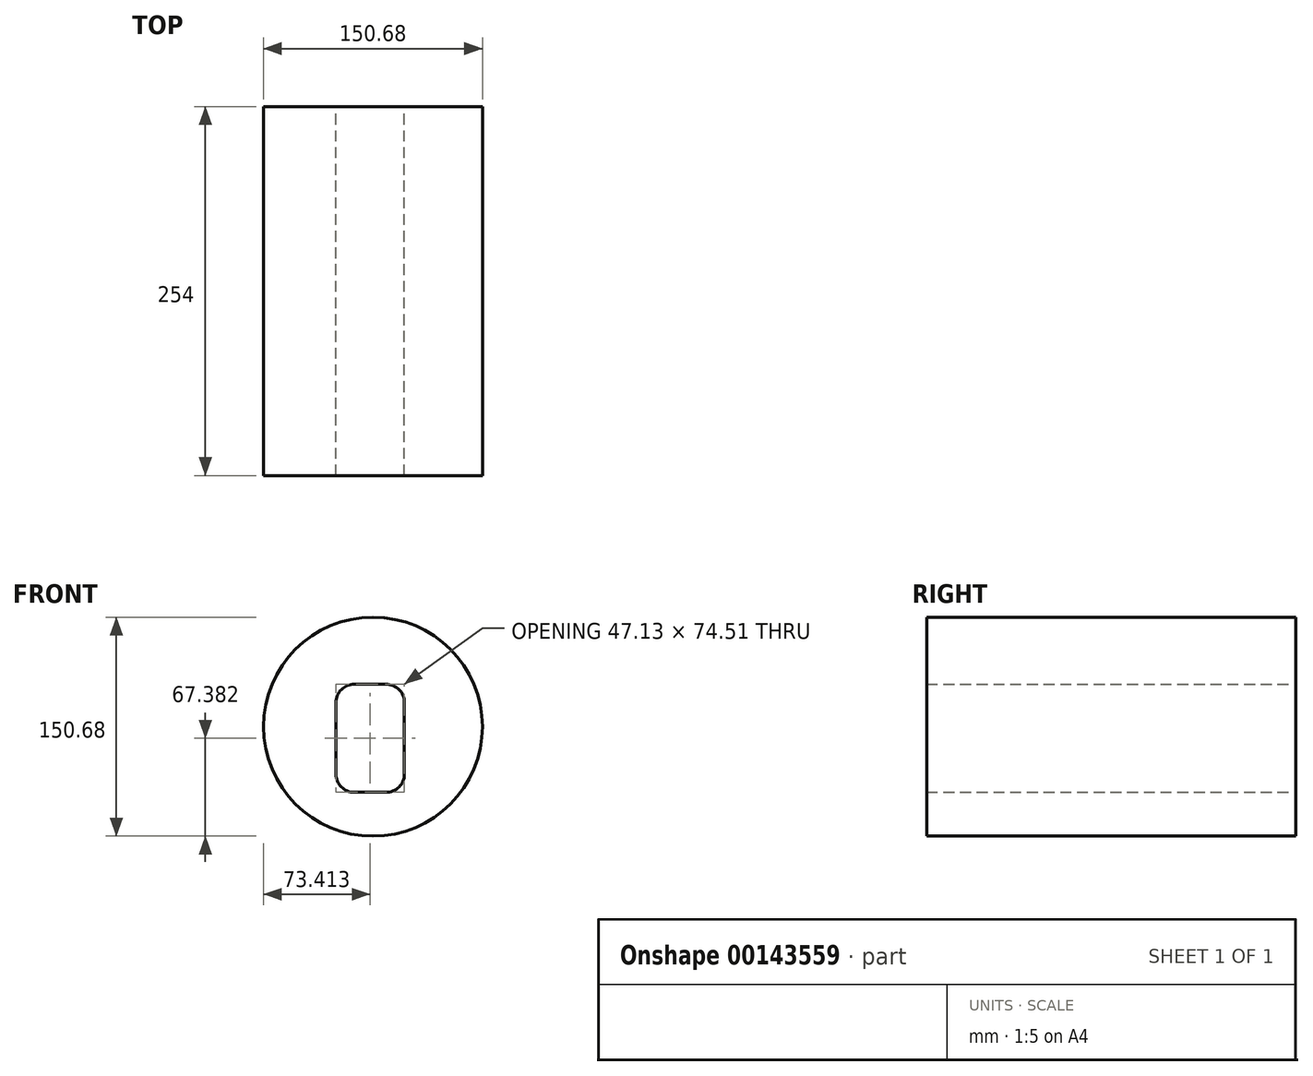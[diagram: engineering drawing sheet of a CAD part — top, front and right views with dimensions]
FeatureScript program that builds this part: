
annotation { "Feature Type Name" : "Feature", "Feature Type Description" : "" }
export const myFeature = defineFeature(function(context is Context, id is Id, definition is map)
    precondition{}
    {
        {
            var Q0;
            Q0=qCreatedBy(makeId("Front.planeOp"),FACE);
            var sketch = newSketch(context, id + "F0", { "sketchPlane" : qUnion([Q0])});
            skCircle(sketch, "E0", {"center": v(0, 0) * mm, "radius": 75.34 * mm});
            skPoint(sketch, "E1.start.orphan", {"position": v(-21.74, 0) * mm});
            skLineSegment(sketch, "E2", {"start": v(0, 0) * mm, "end": v(0, 29.3) * mm});
            skLineSegment(sketch, "E3", {"start": v(0, 29.3) * mm, "end": v(8.94, 29.3) * mm});
            skLineSegment(sketch, "E4", {"start": v(0, 29.3) * mm, "end": v(-12.8, 29.3) * mm});
            skLineSegment(sketch, "E5", {"start": v(21.64, 16.6) * mm, "end": v(21.64, -32.51) * mm});
            skLineSegment(sketch, "E6", {"start": v(8.94, -45.21) * mm, "end": v(-12.8, -45.21) * mm});
            skLineSegment(sketch, "E7", {"start": v(-25.5, -32.51) * mm, "end": v(-25.5, 16.6) * mm});
            skPoint(sketch, "E8.visualSharp", {"position": v(-25.5, 29.3) * mm});
            skArc(sketch, "E8.filletArc", {"start": v(-12.8, 29.3) * mm, "mid": v(-21.77, 25.58) * mm, "end": v(-25.5, 16.6) * mm});
            skPoint(sketch, "E9.visualSharp", {"position": v(21.64, 29.3) * mm});
            skArc(sketch, "E9.filletArc", {"start": v(21.64, 16.6) * mm, "mid": v(17.92, 25.58) * mm, "end": v(8.94, 29.3) * mm});
            skPoint(sketch, "E10.visualSharp", {"position": v(21.64, -45.21) * mm});
            skArc(sketch, "E10.filletArc", {"start": v(8.94, -45.21) * mm, "mid": v(17.92, -41.5) * mm, "end": v(21.64, -32.51) * mm});
            skPoint(sketch, "E11.visualSharp", {"position": v(-25.5, -45.21) * mm});
            skArc(sketch, "E11.filletArc", {"start": v(-25.5, -32.51) * mm, "mid": v(-21.77, -41.5) * mm, "end": v(-12.8, -45.21) * mm});
            skSolve(sketch);
        }
        {
            var Q0;
            Q0 = qSketchRegion(id + "F0", true);
            extrude(context, id + "F1", {"entities" : qUnion([Q0]), "depth" : 254 * mm});
        }
    });
